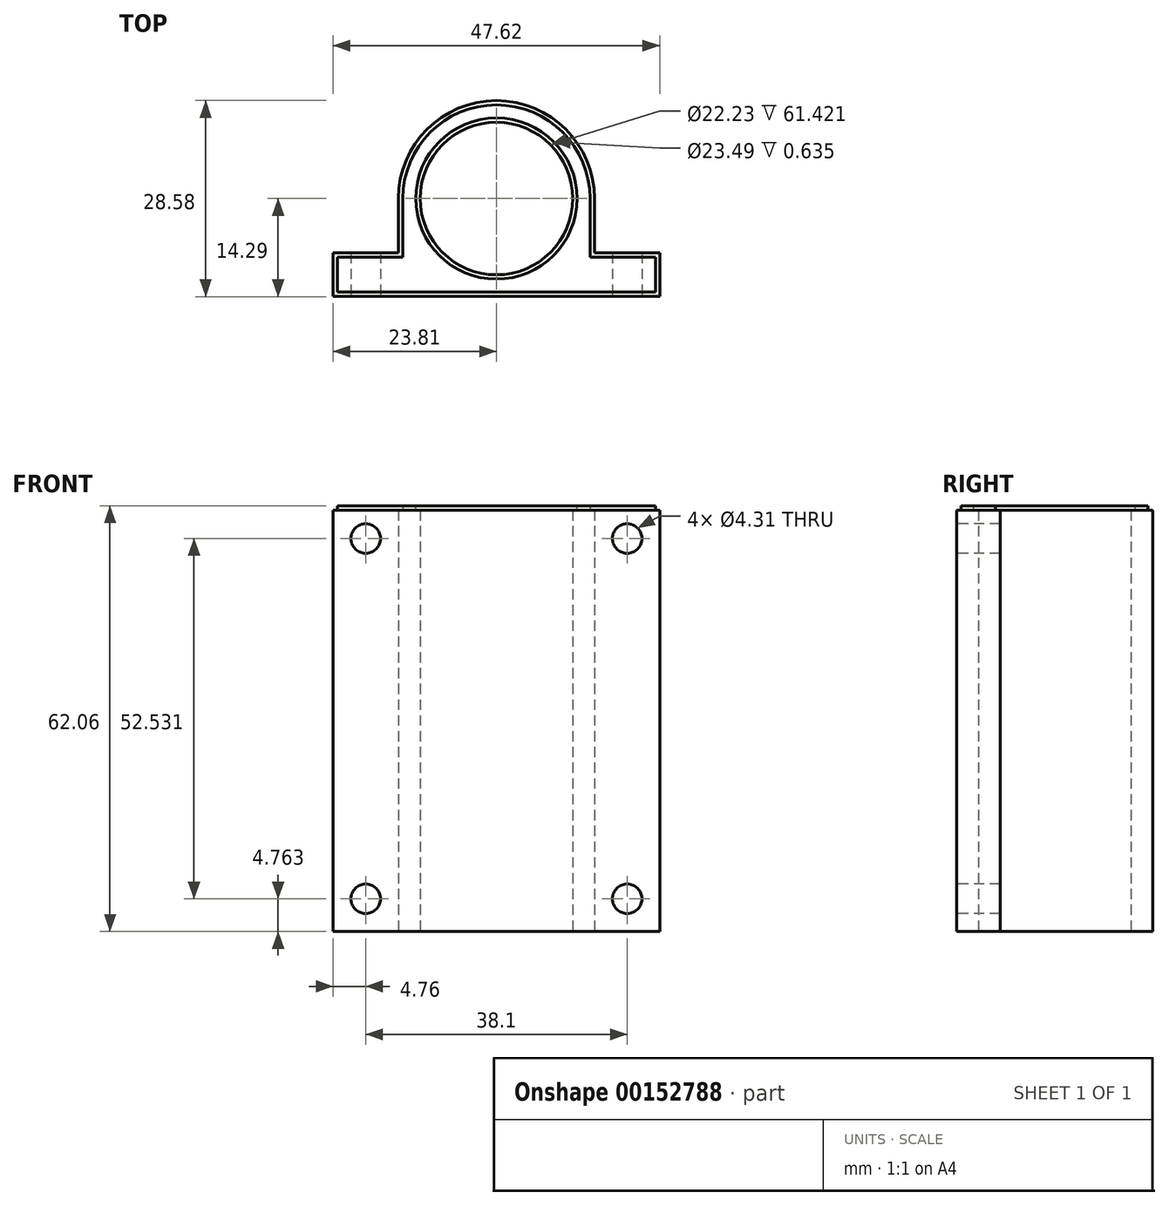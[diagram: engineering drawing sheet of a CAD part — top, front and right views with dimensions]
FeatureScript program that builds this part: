
annotation { "Feature Type Name" : "Feature", "Feature Type Description" : "" }
export const myFeature = defineFeature(function(context is Context, id is Id, definition is map)
    precondition{}
    {
        {
            var Q0;
            Q0=qCreatedBy(makeId("Top.planeOp"),FACE);
            var sketch = newSketch(context, id + "F0", { "sketchPlane" : qUnion([Q0])});
            skCircle(sketch, "E0", {"center": v(0, 0) * mm, "radius": 11.11 * mm});
            skLineSegment(sketch, "E1.bottom", {"start": v(-14.29, 0) * mm, "end": v(14.29, 0) * mm, "construction": true});
            skLineSegment(sketch, "E1.left", {"start": v(-14.29, 0) * mm, "end": v(-14.29, -7.94) * mm});
            skLineSegment(sketch, "E1.right", {"start": v(14.29, 0) * mm, "end": v(14.29, -7.94) * mm});
            skArc(sketch, "E2", {"start": v(14.29, 0) * mm, "mid": v(0, 14.29) * mm, "end": v(-14.29, 0) * mm});
            skLineSegment(sketch, "E3.bottom", {"start": v(-14.29, -7.94) * mm, "end": v(-23.81, -7.94) * mm});
            skLineSegment(sketch, "E3.right", {"start": v(-23.81, -7.94) * mm, "end": v(-23.81, -14.29) * mm});
            skLineSegment(sketch, "E4.bottom", {"start": v(14.29, -7.94) * mm, "end": v(23.81, -7.94) * mm});
            skLineSegment(sketch, "E4.top", {"start": v(-23.81, -14.29) * mm, "end": v(23.81, -14.29) * mm});
            skLineSegment(sketch, "E4.right", {"start": v(23.81, -7.94) * mm, "end": v(23.81, -14.29) * mm});
            skLineSegment(sketch, "E5", {"start": v(0, 0) * mm, "end": v(0, -14.29) * mm, "construction": true});
            skSolve(sketch);
        }
        {
            var Q0;
            Q0 = qSketchRegion(id + "F0", true);
            extrude(context, id + "F1", {"entities" : qUnion([Q0]), "depth" : 62.06 * mm});
        }
        {
            var Q0;
            Q0=makeQuery(id+"F1.opExtrude","SWEPT_FACE",FACE,{"disambiguationData":[OSD([sQuery(id+"F0.wireOp",EDGE,"E4.top")])]});
            var sketch = newSketch(context, id + "F2", { "sketchPlane" : qUnion([Q0])});
            skLineSegment(sketch, "E6.bottom", {"start": v(-23.81, 62.06) * mm, "end": v(-19.05, 62.06) * mm, "construction": true});
            skLineSegment(sketch, "E6.top", {"start": v(-23.81, 57.3) * mm, "end": v(-19.05, 57.3) * mm, "construction": true});
            skLineSegment(sketch, "E6.left", {"start": v(-23.81, 62.06) * mm, "end": v(-23.81, 57.3) * mm, "construction": true});
            skLineSegment(sketch, "E6.right", {"start": v(-19.05, 62.06) * mm, "end": v(-19.05, 57.3) * mm, "construction": true});
            skLineSegment(sketch, "E7", {"start": v(-23.81, 31.03) * mm, "end": v(23.81, 31.03) * mm, "construction": true});
            skLineSegment(sketch, "E8.bottom", {"start": v(-19.05, 57.3) * mm, "end": v(19.05, 57.3) * mm, "construction": true});
            skLineSegment(sketch, "E8.top", {"start": v(-19.05, 4.76) * mm, "end": v(19.05, 4.76) * mm, "construction": true});
            skLineSegment(sketch, "E8.left", {"start": v(-19.05, 57.3) * mm, "end": v(-19.05, 4.76) * mm, "construction": true});
            skLineSegment(sketch, "E8.right", {"start": v(19.05, 57.3) * mm, "end": v(19.05, 4.76) * mm, "construction": true});
            skPoint(sketch, "E8.middle", {"position": v(0, 31.03) * mm});
            skCircle(sketch, "E9", {"center": v(-19.05, 4.76) * mm, "radius": 2.15 * mm});
            skCircle(sketch, "E10", {"center": v(-19.05, 57.3) * mm, "radius": 2.15 * mm});
            skCircle(sketch, "E11", {"center": v(19.05, 57.3) * mm, "radius": 2.15 * mm});
            skCircle(sketch, "E12", {"center": v(19.05, 4.76) * mm, "radius": 2.15 * mm});
            skSolve(sketch);
        }
        {
            var Q0;
            Q0 = qSketchRegion(id + "F2", true);
            var Q1;
            Q1=makeQuery(id+"F1.opExtrude","SWEPT_FACE",FACE,{"disambiguationData":[OSD([sQuery(id+"F0.wireOp",EDGE,"E3.bottom")])]});
            extrude(context, id + "F3", {"entities" : qUnion([Q0]), "operationType" : NewBodyOperationType.REMOVE, "endBound" : BoundingType.UP_TO_SURFACE, "oppositeDirection" : true, "endBoundEntityFace" : qUnion([Q1]), "depth" : 25.4 * mm});
        }
        {
            var Q0;
            Q0=makeQuery(id+"F1.opExtrude","SWEPT_FACE",FACE,{"disambiguationData":[OSD([sQuery(id+"F0.wireOp",EDGE,"E3.right")])]});
            var sketch = newSketch(context, id + "F4", { "sketchPlane" : qUnion([Q0])});
            skLineSegment(sketch, "E13.bottom", {"start": v(14.29, 62.06) * mm, "end": v(13.65, 62.06) * mm});
            skLineSegment(sketch, "E13.top", {"start": v(14.29, 61.42) * mm, "end": v(13.65, 61.42) * mm});
            skLineSegment(sketch, "E13.left", {"start": v(14.29, 62.06) * mm, "end": v(14.29, 61.42) * mm});
            skLineSegment(sketch, "E13.right", {"start": v(13.65, 62.06) * mm, "end": v(13.65, 61.42) * mm});
            skSolve(sketch);
        }
        {
            var Q0;
            Q0=makeQuery(id+"F4.imprint","IMPRINT",FACE,{"disambiguationData":[TD([[makeQuery(id+"F4.imprint","IMPRINT",EDGE,{"derivedFrom":sQuery(id+"F4.wireOp",EDGE,"E13.bottom")}),-1.0]])]});
            var Q1;
            Q1=makeQuery(id+"F1.opExtrude","CAP_EDGE",EDGE,{"disambiguationData":[OSD([sQuery(id+"F0.wireOp",EDGE,"E4.top")])],"isStart":false});
            var Q2;
            Q2=makeQuery(id+"F1.opExtrude","CAP_EDGE",EDGE,{"disambiguationData":[OSD([sQuery(id+"F0.wireOp",EDGE,"E4.right")])],"isStart":false});
            var Q3;
            Q3=makeQuery(id+"F1.opExtrude","CAP_EDGE",EDGE,{"disambiguationData":[OSD([sQuery(id+"F0.wireOp",EDGE,"E4.bottom")])],"isStart":false});
            var Q4;
            Q4=makeQuery(id+"F1.opExtrude","CAP_EDGE",EDGE,{"disambiguationData":[OSD([sQuery(id+"F0.wireOp",EDGE,"E1.right")])],"isStart":false});
            var Q5;
            Q5=makeQuery(id+"F1.opExtrude","CAP_EDGE",EDGE,{"disambiguationData":[OSD([sQuery(id+"F0.wireOp",EDGE,"E2")])],"isStart":false});
            var Q6;
            Q6=makeQuery(id+"F1.opExtrude","CAP_EDGE",EDGE,{"disambiguationData":[OSD([sQuery(id+"F0.wireOp",EDGE,"E1.left")])],"isStart":false});
            var Q7;
            Q7=makeQuery(id+"F1.opExtrude","CAP_EDGE",EDGE,{"disambiguationData":[OSD([sQuery(id+"F0.wireOp",EDGE,"E3.bottom")])],"isStart":false});
            var Q8;
            Q8=makeQuery(id+"F1.opExtrude","CAP_EDGE",EDGE,{"disambiguationData":[OSD([sQuery(id+"F0.wireOp",EDGE,"E3.right")])],"isStart":false});
            sweep(context, id + "F5", {"operationType" : NewBodyOperationType.REMOVE, "profiles" : qUnion([Q0]), "path" : qUnion([Q1, Q2, Q3, Q4, Q5, Q6, Q7, Q8])});
        }
        {
            var Q0;
            Q0=makeQuery(id+"F1.opExtrude","CAP_FACE",FACE,{"disambiguationData":[OSD([sQuery(id+"F0.wireOp",EDGE,"E0"),sQuery(id+"F0.wireOp",EDGE,"E1.left"),sQuery(id+"F0.wireOp",EDGE,"E1.right"),sQuery(id+"F0.wireOp",EDGE,"E2"),sQuery(id+"F0.wireOp",EDGE,"E3.bottom"),sQuery(id+"F0.wireOp",EDGE,"E3.right"),sQuery(id+"F0.wireOp",EDGE,"E4.bottom"),sQuery(id+"F0.wireOp",EDGE,"E4.top"),sQuery(id+"F0.wireOp",EDGE,"E4.right")])],"isStart":false});
            var sketch = newSketch(context, id + "F6", { "sketchPlane" : qUnion([Q0])});
            skCircle(sketch, "E14", {"center": v(0, 0) * mm, "radius": 11.11 * mm});
            skCircle(sketch, "E15", {"center": v(0, 0) * mm, "radius": 11.75 * mm});
            skSolve(sketch);
        }
        {
            var Q0;
            Q0 = qSketchRegion(id + "F6", true);
            var Q1;
            Q1=makeQuery(id+"F5.boolean.opBoolean","COPY",FACE,{"derivedFrom":makeQuery(id+"F5.opSweep","SWEPT_FACE",FACE,{"disambiguationData":[OSD([sQuery(id+"F0.wireOp",EDGE,"E4.top"),sQuery(id+"F4.wireOp",EDGE,"E13.top")])]})});
            extrude(context, id + "F7", {"entities" : qUnion([Q0]), "operationType" : NewBodyOperationType.REMOVE, "endBound" : BoundingType.UP_TO_SURFACE, "oppositeDirection" : true, "endBoundEntityFace" : qUnion([Q1]), "depth" : 25.4 * mm});
        }
    });
